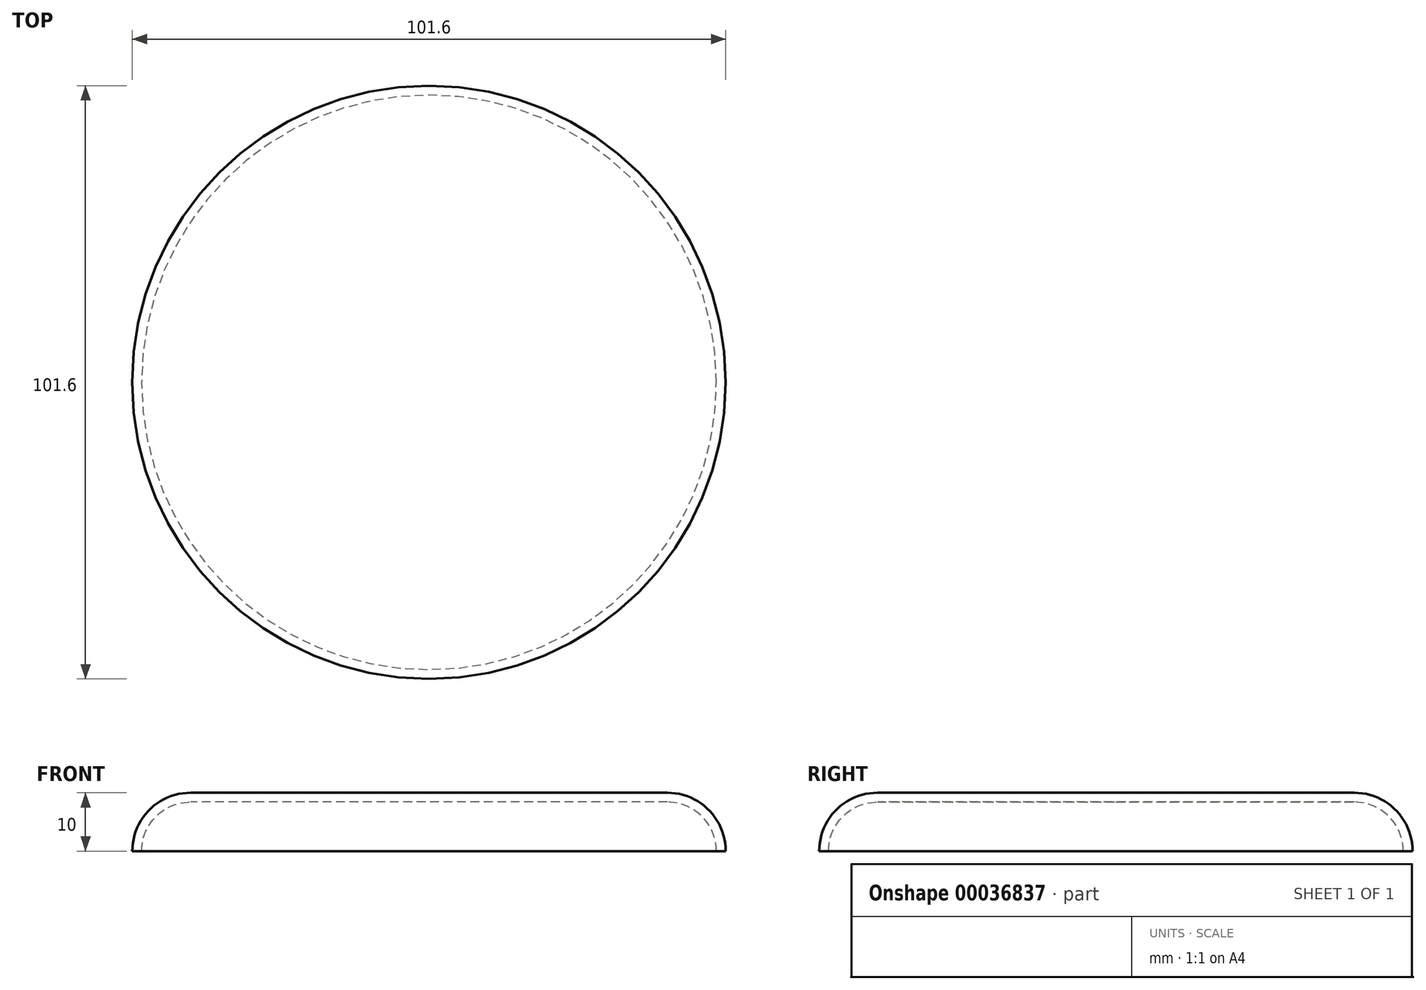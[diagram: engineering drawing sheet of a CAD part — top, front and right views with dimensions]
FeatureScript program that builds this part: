
annotation { "Feature Type Name" : "Feature", "Feature Type Description" : "" }
export const myFeature = defineFeature(function(context is Context, id is Id, definition is map)
    precondition{}
    {
        {
            var Q0;
            Q0=qCreatedBy(makeId("Top.planeOp"),FACE);
            var sketch = newSketch(context, id + "F0", { "sketchPlane" : qUnion([Q0])});
            skCircle(sketch, "E0", {"center": v(0, 0) * mm, "radius": 50.8 * mm});
            skSolve(sketch);
        }
        {
            var Q0;
            Q0=makeQuery(id+"F0.imprint","IMPRINT",FACE,{"disambiguationData":[TD([[makeQuery(id+"F0.imprint","IMPRINT",EDGE,{"derivedFrom":sQuery(id+"F0.wireOp",EDGE,"E0")}),1.0]])]});
            extrude(context, id + "F1", {"entities" : qUnion([Q0]), "depth" : 10 * mm});
        }
        {
            var Q0;
            Q0=makeQuery(id+"F1.opExtrude","CAP_EDGE",EDGE,{"disambiguationData":[OSD([sQuery(id+"F0.wireOp",EDGE,"E0")])],"isStart":false});
            fillet(context, id + "F2", {"entities" : qUnion([Q0]), "radius" : 10 * mm, "tangentPropagation" : true, "allowEdgeOverflow" : false});
        }
        {
            var Q0;
            Q0=makeQuery(id+"F1.opExtrude","CAP_FACE",FACE,{"disambiguationData":[OSD([sQuery(id+"F0.wireOp",EDGE,"E0")])],"isStart":true});
            shell(context, id + "F3", {"entities" : qUnion([Q0]), "thickness" : 1.6 * mm});
        }
    });
